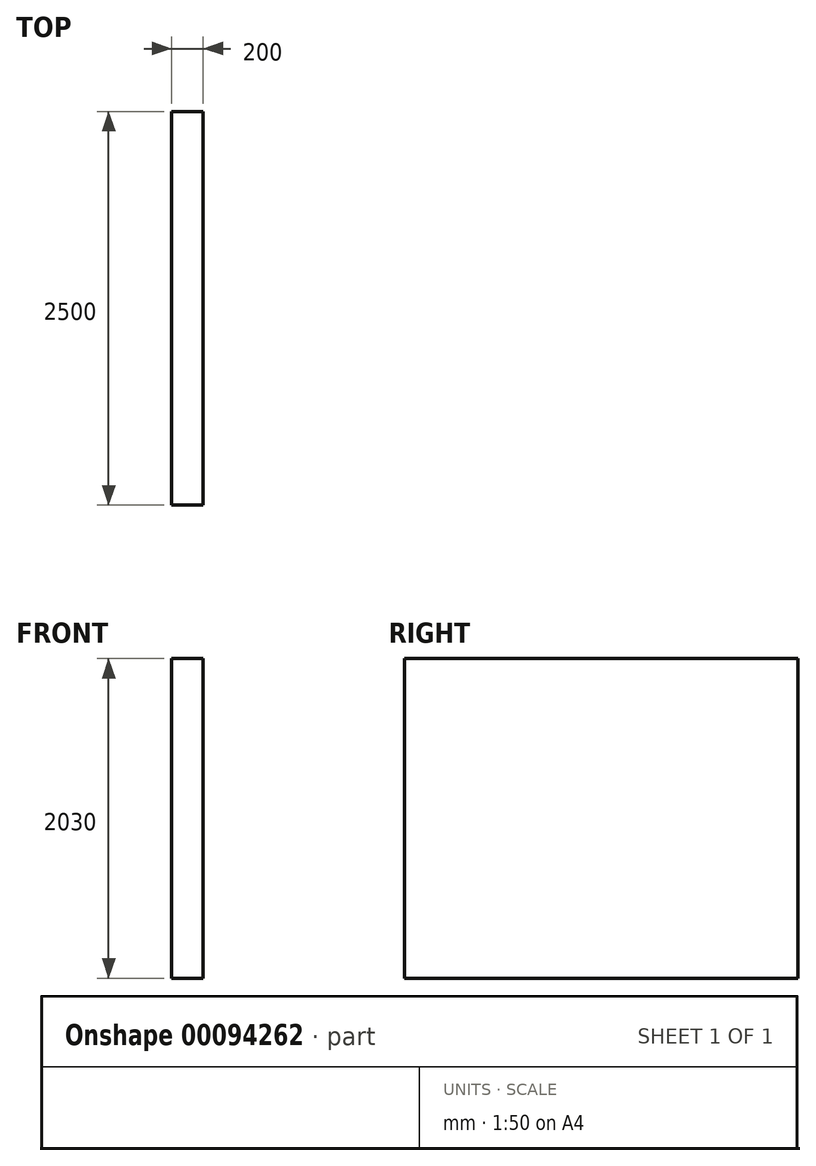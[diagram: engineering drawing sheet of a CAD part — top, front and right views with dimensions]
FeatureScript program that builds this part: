
annotation { "Feature Type Name" : "Feature", "Feature Type Description" : "" }
export const myFeature = defineFeature(function(context is Context, id is Id, definition is map)
    precondition{}
    {
        {
            var Q0;
            Q0=qCreatedBy(makeId("Right.planeOp"),FACE);
            var sketch = newSketch(context, id + "F0", { "sketchPlane" : qUnion([Q0])});
            skLineSegment(sketch, "E0.bottom", {"start": v(0, 0) * mm, "end": v(2500, 0) * mm});
            skLineSegment(sketch, "E0.top", {"start": v(0, -2030) * mm, "end": v(2500, -2030) * mm});
            skLineSegment(sketch, "E0.left", {"start": v(0, 0) * mm, "end": v(0, -2030) * mm});
            skLineSegment(sketch, "E0.right", {"start": v(2500, 0) * mm, "end": v(2500, -2030) * mm});
            skSolve(sketch);
        }
        {
            var Q0;
            Q0 = qSketchRegion(id + "F0", true);
            extrude(context, id + "F1", {"entities" : qUnion([Q0]), "depth" : 200 * mm});
        }
    });
